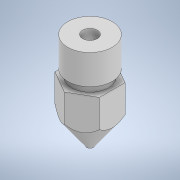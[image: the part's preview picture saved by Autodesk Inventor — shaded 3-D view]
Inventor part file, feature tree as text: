
AUTODESK INVENTOR PART (.ipt)
format: ipt  version: 2022 (Build 260153070, 153G)  size: 150,528 bytes
history: native  units: mm
features: sketch x2, revolve x1, extrude x1
ambient origin geometry x8: Origin, YZ Plane, XZ Plane, XY Plane, X Axis, Y Axis, Z Axis, Center Point
bodies: Solid1 (feature_tree)
feature tree (4):
  revolve  "Revolution1"  [1 undecoded]
  extrude  "Extrusion1"  Depth=6.0mm
  sketch  "Sketch1"  dims[d0=3.0mm d1=13.0mm]
  sketch  "Sketch2"  dims[d2=9.0mm d5=0.45mm d6=2.5mm d7=45.0deg d8=1.0mm d9=0.2mm d10=0.8mm d11=90.0deg d12=3.57735mm d13=8.0mm d14=6.195919mm d15=6.0mm d17=10.0mm d18=8.0mm d19=0.0mm]
note: 1 required parameter value undecoded (feature->parameter linkage not recoverable at this tier; creation-order binding heuristic only, values carry confidence <= 0.55)
